FCSTD DOCUMENT  (FreeCAD 1.1R20260325 (Git shallow))
Label: Stethiscope001
License: All rights reserved
LicenseURL: https://en.wikipedia.org/wiki/All_rights_reserved
objects: App::Point×1, Sketcher::SketchObject×1, PartDesign::Body×1
note: 3 computed .brp shape members not serialized (recipe doc carries the construction recipe); baked Part::Feature solids carry a one-line shape summary decoded from their .brp

FEATURE [App::Point] Origin001
  Role = Origin
FEATURE [Sketcher::SketchObject] Sketch
  ArcFitTolerance = 1e-06
  AttachmentSupport = -> [Origin]
  ExternalTypes = [0]
  FullyConstrained = false
  MakeInternals = false
  MapMode = 5
  _ExternalGeoVersion = 1
  sketch-geometry (8):
    g0: Circle [constr] CenterX=0 CenterY=0 CenterZ=0 NormalX=0 NormalY=0 NormalZ=1 AngleXU=0 Radius=38
    g1: LineSegment [constr] StartX=0 StartY=0 StartZ=0 EndX=26.8701 EndY=26.8701 EndZ=0
    g2: LineSegment [constr] StartX=0 StartY=0 StartZ=0 EndX=-26.87 EndY=26.8701 EndZ=0
    g3: LineSegment [constr] StartX=0 StartY=0 StartZ=0 EndX=0 EndY=-38 EndZ=0
    g4: Circle CenterX=13.435 CenterY=13.435 CenterZ=0 NormalX=0 NormalY=0 NormalZ=1 AngleXU=0 Radius=19
    g5: ArcOfCircle CenterX=0 CenterY=-19 CenterZ=0 NormalX=0 NormalY=0 NormalZ=1 AngleXU=0 Radius=19 StartAngle=3.07371 EndAngle=7.85398
    g6: ArcOfCircle CenterX=-13.435 CenterY=13.435 CenterZ=0 NormalX=0 NormalY=0 NormalZ=1 AngleXU=0 Radius=19 StartAngle=5.49779 EndAngle=10.2781
    g7: ArcOfCircle CenterX=-39.4031 CenterY=-16.3213 CenterZ=0 NormalX=0 NormalY=0 NormalZ=1 AngleXU=0 Radius=20.494 StartAngle=6.21531 EndAngle=7.13646
  constraints (20):
    c: Diameter(g0) = 76
    c: Coincident(g0,g-1)
    c: Angle(g-1,g1) = 0.785398
    c: Coincident(g1,g0)
    c: PointOnObject(g1,g0)
    c: Distance(g2) = 38
    c: Angle(g-1,g2) = 2.35619
    c: Coincident(g2,g0)
    c: Coincident(g3,g0)
    c: PointOnObject(g3,g0)
    c: Vertical(g3)
    c: Symmetric(g1,g1,g4)
    c: PointOnObject(g1,g4)
    c: Symmetric(g3,g3,g5)
    c: Symmetric(g2,g2,g6)
    c: Tangent(g7,g6) = 1.5708
    c: Tangent(g7,g5) = 1.5708
    c: PointOnObject(g0,g5)
    c: PointOnObject(g5,g4)
    c: Coincident(g6,g5)
FEATURE [PartDesign::Body] Body
  AllowCompound = true
  Group = -> [Sketch]
  Origin = -> Origin
